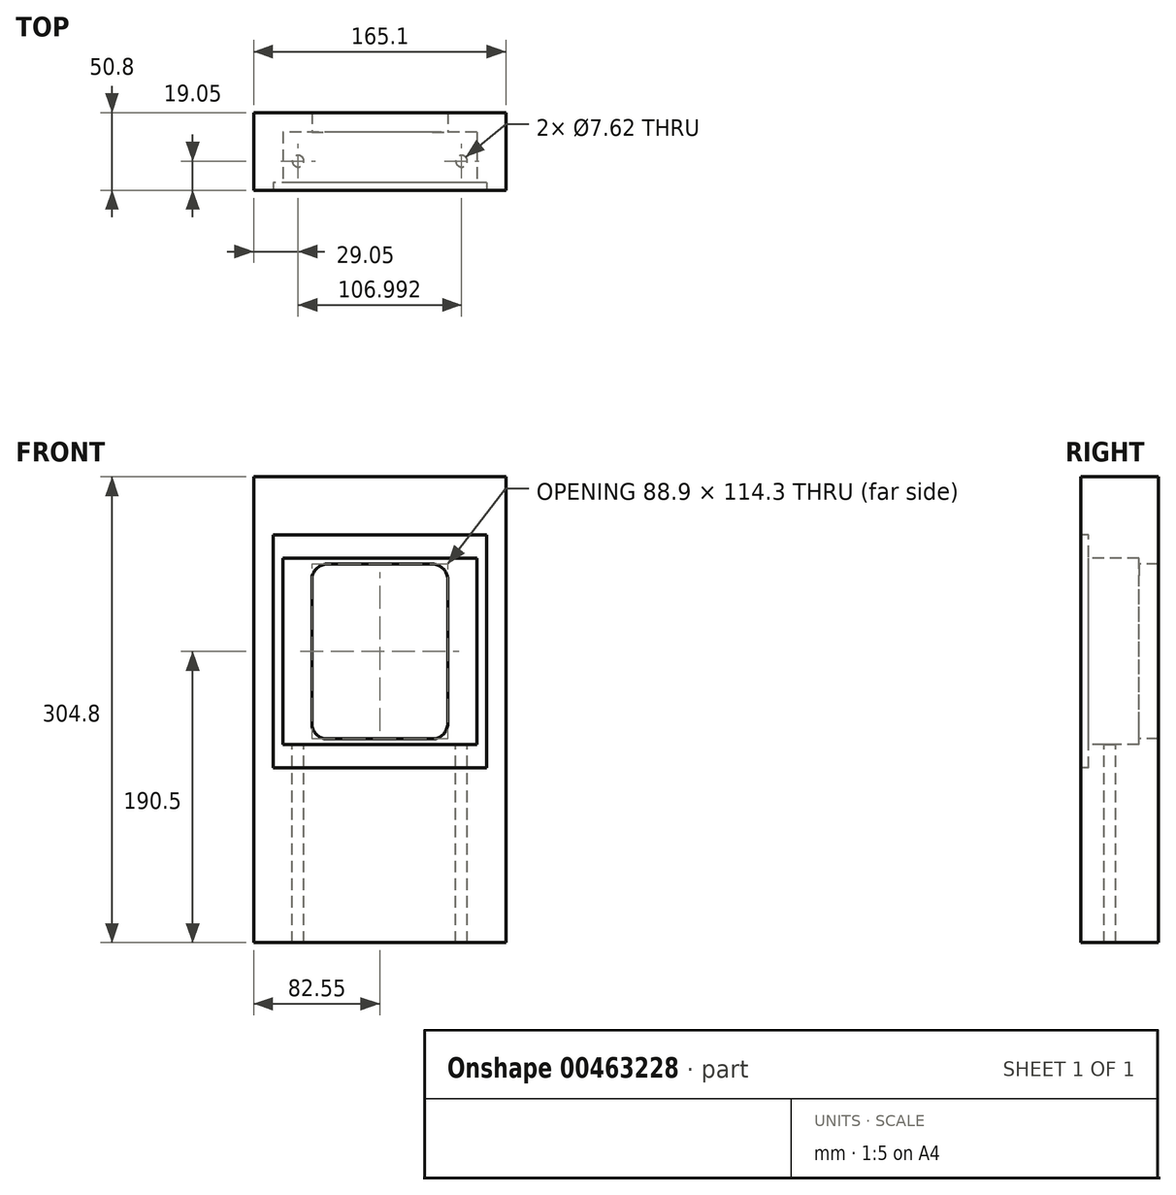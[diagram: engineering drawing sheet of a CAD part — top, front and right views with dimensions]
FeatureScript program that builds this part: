
annotation { "Feature Type Name" : "Feature", "Feature Type Description" : "" }
export const myFeature = defineFeature(function(context is Context, id is Id, definition is map)
    precondition{}
    {
        {
            var Q0;
            Q0=qCreatedBy(makeId("Front.planeOp"),FACE);
            var sketch = newSketch(context, id + "F0", { "sketchPlane" : qUnion([Q0])});
            skLineSegment(sketch, "E0.top", {"start": v(82.55, 114.3) * mm, "end": v(-82.55, 114.3) * mm});
            skLineSegment(sketch, "E0.left", {"start": v(82.55, -190.5) * mm, "end": v(82.55, 114.3) * mm});
            skLineSegment(sketch, "E0.right", {"start": v(-82.55, -190.5) * mm, "end": v(-82.55, 114.3) * mm});
            skPoint(sketch, "E0.middle", {"position": v(0, 0) * mm});
            skLineSegment(sketch, "E1.bottom", {"start": v(69.85, -76.2) * mm, "end": v(-69.85, -76.2) * mm});
            skLineSegment(sketch, "E1.top", {"start": v(69.85, 76.2) * mm, "end": v(-69.85, 76.2) * mm});
            skLineSegment(sketch, "E1.left", {"start": v(69.85, -76.2) * mm, "end": v(69.85, 76.2) * mm});
            skLineSegment(sketch, "E1.right", {"start": v(-69.85, -76.2) * mm, "end": v(-69.85, 76.2) * mm});
            skLineSegment(sketch, "E2.bottom", {"start": v(63.5, -60.96) * mm, "end": v(-63.5, -60.96) * mm});
            skLineSegment(sketch, "E2.top", {"start": v(63.5, 60.96) * mm, "end": v(-63.5, 60.96) * mm});
            skLineSegment(sketch, "E2.left", {"start": v(63.5, -60.96) * mm, "end": v(63.5, 60.96) * mm});
            skLineSegment(sketch, "E2.right", {"start": v(-63.5, -60.96) * mm, "end": v(-63.5, 60.96) * mm});
            skLineSegment(sketch, "E3.bottom", {"start": v(44.45, -57.15) * mm, "end": v(-44.45, -57.15) * mm});
            skLineSegment(sketch, "E3.top", {"start": v(44.45, 57.15) * mm, "end": v(-44.45, 57.15) * mm});
            skLineSegment(sketch, "E3.left", {"start": v(44.45, -57.15) * mm, "end": v(44.45, 57.15) * mm});
            skLineSegment(sketch, "E3.right", {"start": v(-44.45, -57.15) * mm, "end": v(-44.45, 57.15) * mm});
            skLineSegment(sketch, "E4", {"start": v(-82.55, -190.5) * mm, "end": v(82.55, -190.5) * mm});
            skPoint(sketch, "E5.orphan", {"position": v(-82.55, -114.3) * mm});
            skPoint(sketch, "E6.orphan", {"position": v(82.55, -114.3) * mm});
            skSolve(sketch);
        }
        {
            var Q0;
            Q0=makeQuery(id+"F0.imprint","IMPRINT",FACE,{"disambiguationData":[TD([[makeQuery(id+"F0.imprint","IMPRINT",EDGE,{"derivedFrom":sQuery(id+"F0.wireOp",EDGE,"E0.top")}),1.0]])]});
            var Q1;
            Q1=makeQuery(id+"F0.imprint","IMPRINT",FACE,{"disambiguationData":[TD([[makeQuery(id+"F0.imprint","IMPRINT",EDGE,{"derivedFrom":sQuery(id+"F0.wireOp",EDGE,"E1.bottom")}),-1.0]])]});
            var Q2;
            Q2=makeQuery(id+"F0.imprint","IMPRINT",FACE,{"disambiguationData":[TD([[makeQuery(id+"F0.imprint","IMPRINT",EDGE,{"derivedFrom":sQuery(id+"F0.wireOp",EDGE,"E2.bottom")}),-1.0]])]});
            var Q3;
            {var subQ0=sQuery(id+"F0.wireOp",EDGE,"dQK7Thth-TP6K-kbBQ-5Cwl-0GHNaYrmpQfn.left");var subQ1=sQuery(id+"F0.wireOp",EDGE,"E1.bottom");var subQ2=makeQuery(id+"F0.imprint","INTERSECT",VERTEX,{"derivedFrom":[subQ1,subQ0]});Q3=makeQuery(id+"F0.imprint","IMPRINT",FACE,{"disambiguationData":[TD([[makeQuery(id+"F0.imprint","IMPRINT",EDGE,{"disambiguationData":[TD([[subQ2,-1.0]])],"derivedFrom":subQ1}),1.0]])]});}
            var Q4;
            {var subQ5=sQuery(id+"F0.wireOp",EDGE,"huDVYpq4-8GHm-f6ov-cYvV-LWDsyoBmHsaB.top");Q4=makeQuery(id+"F0.imprint","IMPRINT",FACE,{"disambiguationData":[TD([[makeQuery(id+"F0.imprint","IMPRINT",EDGE,{"derivedFrom":subQ5}),1.0]])]});}
            var Q5;
            {var subQ5=sQuery(id+"F0.wireOp",EDGE,"dQK7Thth-TP6K-kbBQ-5Cwl-0GHNaYrmpQfn.bottom");Q5=makeQuery(id+"F0.imprint","IMPRINT",FACE,{"disambiguationData":[TD([[makeQuery(id+"F0.imprint","IMPRINT",EDGE,{"derivedFrom":subQ5}),-1.0]])]});}
            var Q6;
            {var subQ5=sQuery(id+"F0.wireOp",EDGE,"dQK7Thth-TP6K-kbBQ-5Cwl-0GHNaYrmpQfn.top");Q6=makeQuery(id+"F0.imprint","IMPRINT",FACE,{"disambiguationData":[TD([[makeQuery(id+"F0.imprint","IMPRINT",EDGE,{"derivedFrom":subQ5}),1.0]])]});}
            var Q7;
            {var subQ5=sQuery(id+"F0.wireOp",EDGE,"huDVYpq4-8GHm-f6ov-cYvV-LWDsyoBmHsaB.bottom");Q7=makeQuery(id+"F0.imprint","IMPRINT",FACE,{"disambiguationData":[TD([[makeQuery(id+"F0.imprint","IMPRINT",EDGE,{"derivedFrom":subQ5}),-1.0]])]});}
            var Q8;
            {var subQ0=sQuery(id+"F0.wireOp",EDGE,"dQK7Thth-TP6K-kbBQ-5Cwl-0GHNaYrmpQfn.left");var subQ1=sQuery(id+"F0.wireOp",EDGE,"E1.bottom");var subQ2=makeQuery(id+"F0.imprint","INTERSECT",VERTEX,{"derivedFrom":[subQ1,subQ0]});Q8=makeQuery(id+"F0.imprint","IMPRINT",FACE,{"disambiguationData":[TD([[makeQuery(id+"F0.imprint","IMPRINT",EDGE,{"disambiguationData":[TD([[subQ2,-1.0]])],"derivedFrom":subQ1}),-1.0]])]});}
            extrude(context, id + "F1", {"entities" : qUnion([Q0, Q1, Q2, Q3, Q4, Q5, Q6, Q7, Q8]), "oppositeDirection" : true, "depth" : 50.8 * mm});
        }
        {
            var Q0;
            Q0=makeQuery(id+"F0.imprint","IMPRINT",FACE,{"disambiguationData":[TD([[makeQuery(id+"F0.imprint","IMPRINT",EDGE,{"derivedFrom":sQuery(id+"F0.wireOp",EDGE,"E1.bottom")}),-1.0]])]});
            var Q1;
            {var subQ5=sQuery(id+"F0.wireOp",EDGE,"huDVYpq4-8GHm-f6ov-cYvV-LWDsyoBmHsaB.bottom");Q1=makeQuery(id+"F0.imprint","IMPRINT",FACE,{"disambiguationData":[TD([[makeQuery(id+"F0.imprint","IMPRINT",EDGE,{"derivedFrom":subQ5}),-1.0]])]});}
            var Q2;
            {var subQ0=sQuery(id+"F0.wireOp",EDGE,"dQK7Thth-TP6K-kbBQ-5Cwl-0GHNaYrmpQfn.left");var subQ1=sQuery(id+"F0.wireOp",EDGE,"E1.bottom");var subQ2=makeQuery(id+"F0.imprint","INTERSECT",VERTEX,{"derivedFrom":[subQ1,subQ0]});Q2=makeQuery(id+"F0.imprint","IMPRINT",FACE,{"disambiguationData":[TD([[makeQuery(id+"F0.imprint","IMPRINT",EDGE,{"disambiguationData":[TD([[subQ2,-1.0]])],"derivedFrom":subQ1}),-1.0]])]});}
            var Q3;
            {var subQ5=sQuery(id+"F0.wireOp",EDGE,"dQK7Thth-TP6K-kbBQ-5Cwl-0GHNaYrmpQfn.bottom");Q3=makeQuery(id+"F0.imprint","IMPRINT",FACE,{"disambiguationData":[TD([[makeQuery(id+"F0.imprint","IMPRINT",EDGE,{"derivedFrom":subQ5}),-1.0]])]});}
            extrude(context, id + "F2", {"entities" : qUnion([Q0, Q1, Q2, Q3]), "operationType" : NewBodyOperationType.REMOVE, "oppositeDirection" : true, "depth" : 5 * mm});
        }
        {
            var Q0;
            Q0=makeQuery(id+"F0.imprint","IMPRINT",FACE,{"disambiguationData":[TD([[makeQuery(id+"F0.imprint","IMPRINT",EDGE,{"derivedFrom":sQuery(id+"F0.wireOp",EDGE,"E2.bottom")}),-1.0]])]});
            extrude(context, id + "F3", {"entities" : qUnion([Q0]), "operationType" : NewBodyOperationType.REMOVE, "oppositeDirection" : true, "depth" : 38.1 * mm});
        }
        {
            var Q0;
            Q0=makeQuery(id+"F1.opExtrude","SWEPT_EDGE",EDGE,{"disambiguationData":[OSD([sQuery(id+"F0.wireOp",EDGE,"E3.top"),sQuery(id+"F0.wireOp",EDGE,"E3.right")])]});
            var Q1;
            Q1=makeQuery(id+"F1.opExtrude","SWEPT_EDGE",EDGE,{"disambiguationData":[OSD([sQuery(id+"F0.wireOp",EDGE,"E3.top"),sQuery(id+"F0.wireOp",EDGE,"E3.left")])]});
            var Q2;
            Q2=makeQuery(id+"F1.opExtrude","SWEPT_EDGE",EDGE,{"disambiguationData":[OSD([sQuery(id+"F0.wireOp",EDGE,"E3.bottom"),sQuery(id+"F0.wireOp",EDGE,"E3.right")])]});
            var Q3;
            Q3=makeQuery(id+"F1.opExtrude","SWEPT_EDGE",EDGE,{"disambiguationData":[OSD([sQuery(id+"F0.wireOp",EDGE,"E3.bottom"),sQuery(id+"F0.wireOp",EDGE,"E3.left")])]});
            fillet(context, id + "F4", {"entities" : qUnion([Q0, Q1, Q2, Q3]), "radius" : 10 * mm, "tangentPropagation" : true, "allowEdgeOverflow" : false});
        }
        {
            var Q0;
            Q0=makeQuery(id+"F3.boolean.opBoolean","COPY",FACE,{"derivedFrom":makeQuery(id+"F3.opExtrude","SWEPT_FACE",FACE,{"disambiguationData":[OSD([sQuery(id+"F0.wireOp",EDGE,"E2.bottom")])]})});
            var sketch = newSketch(context, id + "F5", { "sketchPlane" : qUnion([Q0])});
            skCircle(sketch, "E7", {"center": v(53.5, 19.05) * mm, "radius": 3.81 * mm});
            skCircle(sketch, "E8", {"center": v(-53.5, 19.05) * mm, "radius": 3.81 * mm});
            skLineSegment(sketch, "E9", {"start": v(-90.8, 19.05) * mm, "end": v(116.51, 19.05) * mm, "construction": true});
            skSolve(sketch);
        }
        {
            var Q0;
            Q0=makeQuery(id+"F5.imprint","IMPRINT",FACE,{"disambiguationData":[TD([[makeQuery(id+"F5.imprint","IMPRINT",EDGE,{"derivedFrom":sQuery(id+"F5.wireOp",EDGE,"E8")}),1.0]])]});
            var Q1;
            Q1=makeQuery(id+"F5.imprint","IMPRINT",FACE,{"disambiguationData":[TD([[makeQuery(id+"F5.imprint","IMPRINT",EDGE,{"derivedFrom":sQuery(id+"F5.wireOp",EDGE,"E7")}),1.0]])]});
            extrude(context, id + "F6", {"entities" : qUnion([Q0, Q1]), "operationType" : NewBodyOperationType.REMOVE, "endBound" : BoundingType.UP_TO_NEXT, "oppositeDirection" : true, "depth" : 25.4 * mm});
        }
    });
